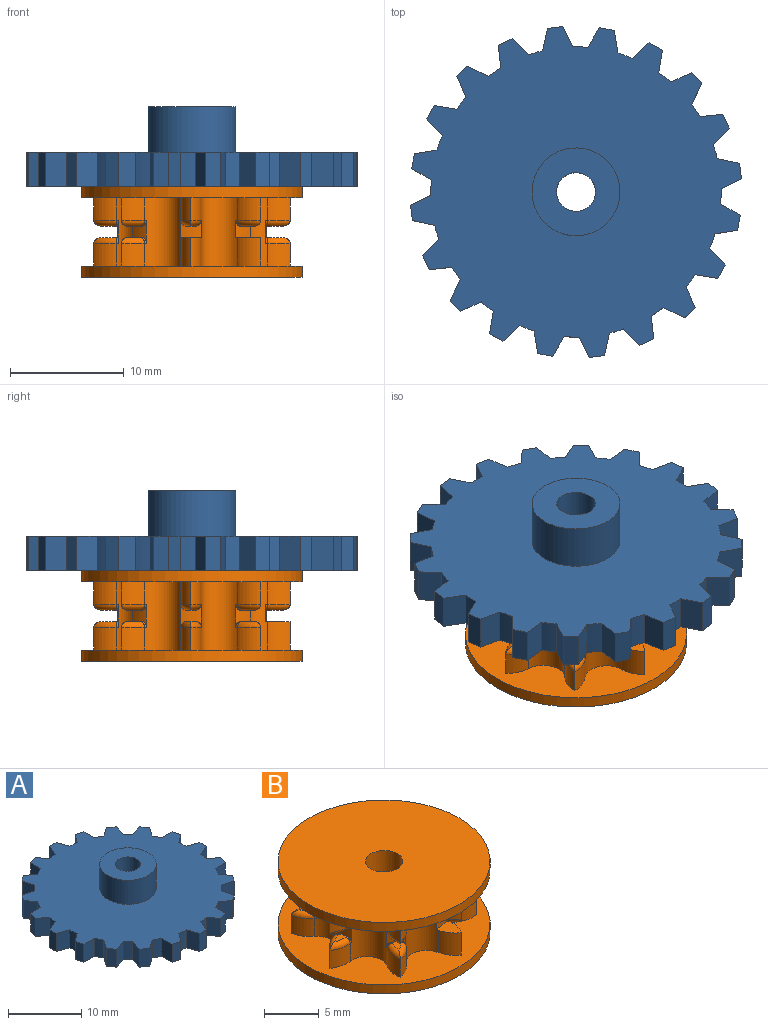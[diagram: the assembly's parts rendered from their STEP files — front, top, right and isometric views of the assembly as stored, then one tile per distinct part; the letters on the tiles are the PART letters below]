
ASSEMBLY  parts=2 mates=1
PART A: 85 faces, bbox 29.1x29.1x7 mm
  f0: plane 3x1.89mm, normal (-0.94,0.33,0), area 6mm2, adj f2,f3,f4,f5
  f1: plane 3x1.89mm, normal (0.94,0.33,0), area 6mm2, adj f2,f3,f4,f81
  f2: plane 3x1.33mm, normal (0,1,0), area 4mm2, adj f0,f1,f3,f4
  f3: plane 29.1x29.1mm, normal (0,0,1), area 535.5mm2, adj f0,f1,f2,f5,f6,f7,f8,f9
  f4: plane 29.1x29.1mm, normal (0,0,-1), area 573.2mm2, adj f0,f1,f2,f5,f6,f7,f8,f9
  f5: cylinder r=12.73mm len=3mm, axis (0,0,-1), area 4mm2, adj f0,f3,f4,f7
  f6: plane 3x2mm, normal (-1,0.03,0), area 6mm2, adj f3,f4,f8,f9
  f7: plane 3x1.59mm, normal (0.79,0.61,0), area 6mm2, adj f3,f4,f5,f8
  f8: plane 3x1.27mm, normal (-0.31,0.95,0), area 4mm2, adj f3,f4,f6,f7
  f9: cylinder r=12.73mm len=3mm, axis (0,0,-1), area 4mm2, adj f3,f4,f6,f11
  f10: plane 3x1.92mm, normal (-0.96,-0.28,0), area 6mm2, adj f3,f4,f12,f13
  f11: plane 3x1.65mm, normal (0.57,0.82,0), area 6mm2, adj f3,f4,f9,f12
  f12: plane 3x1.08mm, normal (-0.59,0.81,0), area 4mm2, adj f3,f4,f10,f11
  f13: cylinder r=12.73mm len=3mm, axis (0,0,-1), area 4mm2, adj f3,f4,f10,f15
  f14: plane 3x1.65mm, normal (-0.82,-0.57,0), area 6mm2, adj f3,f4,f16,f17
  f15: plane 3x1.92mm, normal (0.28,0.96,0), area 6mm2, adj f3,f4,f13,f16
  f16: plane 3x1.08mm, normal (-0.81,0.59,0), area 4mm2, adj f3,f4,f14,f15
  f17: cylinder r=12.73mm len=3mm, axis (0,0,-1), area 4mm2, adj f3,f4,f14,f19
  f18: plane 3x1.59mm, normal (-0.61,-0.79,0), area 6mm2, adj f3,f4,f20,f21
  f19: plane 3x2mm, normal (-0.03,1,0), area 6mm2, adj f3,f4,f17,f20
  f20: plane 3x1.27mm, normal (-0.95,0.31,0), area 4mm2, adj f3,f4,f18,f19
  f21: cylinder r=12.73mm len=3mm, axis (0,0,-1), area 4mm2, adj f3,f4,f18,f23
  f22: plane 3x1.89mm, normal (-0.33,-0.94,0), area 6mm2, adj f3,f4,f24,f25
  f23: plane 3x1.89mm, normal (-0.33,0.94,0), area 6mm2, adj f3,f4,f21,f24
  f24: plane 3x1.33mm, normal (-1,0,0), area 4mm2, adj f3,f4,f22,f23
  f25: cylinder r=12.73mm len=3mm, axis (0,0,-1), area 4mm2, adj f3,f4,f22,f27
  f26: plane 3x2mm, normal (-0.03,-1,0), area 6mm2, adj f3,f4,f28,f29
  f27: plane 3x1.59mm, normal (-0.61,0.79,0), area 6mm2, adj f3,f4,f25,f28
  f28: plane 3x1.27mm, normal (-0.95,-0.31,0), area 4mm2, adj f3,f4,f26,f27
  f29: cylinder r=12.73mm len=3mm, axis (0,0,-1), area 4mm2, adj f3,f4,f26,f31
  f30: plane 3x1.92mm, normal (0.28,-0.96,0), area 6mm2, adj f3,f4,f32,f33
  f31: plane 3x1.65mm, normal (-0.82,0.57,0), area 6mm2, adj f3,f4,f29,f32
  f32: plane 3x1.08mm, normal (-0.81,-0.59,0), area 4mm2, adj f3,f4,f30,f31
  f33: cylinder r=12.73mm len=3mm, axis (0,0,-1), area 4mm2, adj f3,f4,f30,f35
  f34: plane 3x1.65mm, normal (0.57,-0.82,0), area 6mm2, adj f3,f4,f36,f37
  f35: plane 3x1.92mm, normal (-0.96,0.28,0), area 6mm2, adj f3,f4,f33,f36
  f36: plane 3x1.08mm, normal (-0.59,-0.81,0), area 4mm2, adj f3,f4,f34,f35
  f37: cylinder r=12.73mm len=3mm, axis (0,0,-1), area 4mm2, adj f3,f4,f34,f39
  f38: plane 3x1.59mm, normal (0.79,-0.61,0), area 6mm2, adj f3,f4,f40,f41
  f39: plane 3x2mm, normal (-1,-0.03,0), area 6mm2, adj f3,f4,f37,f40
  f40: plane 3x1.27mm, normal (-0.31,-0.95,0), area 4mm2, adj f3,f4,f38,f39
  f41: cylinder r=12.73mm len=3mm, axis (0,0,-1), area 4mm2, adj f3,f4,f38,f43
  f42: plane 3x1.89mm, normal (0.94,-0.33,0), area 6mm2, adj f3,f4,f44,f45
  f43: plane 3x1.89mm, normal (-0.94,-0.33,0), area 6mm2, adj f3,f4,f41,f44
  f44: plane 3x1.33mm, normal (0,-1,0), area 4mm2, adj f3,f4,f42,f43
  f45: cylinder r=12.73mm len=3mm, axis (0,0,-1), area 4mm2, adj f3,f4,f42,f47
  f46: plane 3x2mm, normal (1,-0.03,0), area 6mm2, adj f3,f4,f48,f49
  f47: plane 3x1.59mm, normal (-0.79,-0.61,0), area 6mm2, adj f3,f4,f45,f48
  f48: plane 3x1.27mm, normal (0.31,-0.95,0), area 4mm2, adj f3,f4,f46,f47
  f49: cylinder r=12.73mm len=3mm, axis (0,0,-1), area 4mm2, adj f3,f4,f46,f51
  f50: plane 3x1.92mm, normal (0.96,0.28,0), area 6mm2, adj f3,f4,f52,f53
  f51: plane 3x1.65mm, normal (-0.57,-0.82,0), area 6mm2, adj f3,f4,f49,f52
  f52: plane 3x1.08mm, normal (0.59,-0.81,0), area 4mm2, adj f3,f4,f50,f51
  f53: cylinder r=12.73mm len=3mm, axis (0,0,-1), area 4mm2, adj f3,f4,f50,f55
  f54: plane 3x1.65mm, normal (0.82,0.57,0), area 6mm2, adj f3,f4,f56,f57
  f55: plane 3x1.92mm, normal (-0.28,-0.96,0), area 6mm2, adj f3,f4,f53,f56
  f56: plane 3x1.08mm, normal (0.81,-0.59,0), area 4mm2, adj f3,f4,f54,f55
  f57: cylinder r=12.73mm len=3mm, axis (0,0,-1), area 4mm2, adj f3,f4,f54,f59
  f58: plane 3x1.59mm, normal (0.61,0.79,0), area 6mm2, adj f3,f4,f60,f61
  f59: plane 3x2mm, normal (0.03,-1,0), area 6mm2, adj f3,f4,f57,f60
  f60: plane 3x1.27mm, normal (0.95,-0.31,0), area 4mm2, adj f3,f4,f58,f59
  f61: cylinder r=12.73mm len=3mm, axis (0,0,-1), area 4mm2, adj f3,f4,f58,f63
  f62: plane 3x1.89mm, normal (0.33,0.94,0), area 6mm2, adj f3,f4,f64,f65
  f63: plane 3x1.89mm, normal (0.33,-0.94,0), area 6mm2, adj f3,f4,f61,f64
  f64: plane 3x1.33mm, normal (1,0,0), area 4mm2, adj f3,f4,f62,f63
  f65: cylinder r=12.73mm len=3mm, axis (0,0,-1), area 4mm2, adj f3,f4,f62,f67
  f66: plane 3x2mm, normal (0.03,1,0), area 6mm2, adj f3,f4,f68,f69
  f67: plane 3x1.59mm, normal (0.61,-0.79,0), area 6mm2, adj f3,f4,f65,f68
  f68: plane 3x1.27mm, normal (0.95,0.31,0), area 4mm2, adj f3,f4,f66,f67
  f69: cylinder r=12.73mm len=3mm, axis (0,0,-1), area 4mm2, adj f3,f4,f66,f71
  f70: plane 3x1.92mm, normal (-0.28,0.96,0), area 6mm2, adj f3,f4,f72,f73
  f71: plane 3x1.65mm, normal (0.82,-0.57,0), area 6mm2, adj f3,f4,f69,f72
  f72: plane 3x1.08mm, normal (0.81,0.59,0), area 4mm2, adj f3,f4,f70,f71
  f73: cylinder r=12.73mm len=3mm, axis (0,0,-1), area 4mm2, adj f3,f4,f70,f75
  f74: plane 3x1.65mm, normal (-0.57,0.82,0), area 6mm2, adj f3,f4,f76,f77
  f75: plane 3x1.92mm, normal (0.96,-0.28,0), area 6mm2, adj f3,f4,f73,f76
  f76: plane 3x1.08mm, normal (0.59,0.81,0), area 4mm2, adj f3,f4,f74,f75
  f77: cylinder r=12.73mm len=3mm, axis (0,0,-1), area 4mm2, adj f3,f4,f74,f79
  f78: plane 3x1.59mm, normal (-0.79,0.61,0), area 6mm2, adj f3,f4,f80,f81
  f79: plane 3x2mm, normal (1,0.03,0), area 6mm2, adj f3,f4,f77,f80
  f80: plane 3x1.27mm, normal (0.31,0.95,0), area 4mm2, adj f3,f4,f78,f79
  f81: cylinder r=12.73mm len=3mm, axis (0,0,-1), area 4mm2, adj f1,f3,f4,f78
  f82: cylinder r=1.7mm len=7mm, axis (0,0,-1), area 74.8mm2, adj f4,f84
  f83: cylinder r=3.86mm len=7.71mm, axis (0,0,-1), area 96.9mm2, adj f3,f84
  f84: plane 7.71x7.71mm, normal (0,0,1), area 37.7mm2, adj f82,f83
PART B: 127 faces, bbox 19.4x19.4x8 mm
  f0: cylinder r=2.85mm len=2.12mm, axis (0,0,1), area 4.4mm2, adj f2,f23,f42,f92
  f1: cylinder r=2.85mm len=2.09mm, axis (0,0,1), area 4.4mm2, adj f2,f3,f42,f72
  f2: cylinder r=1.9mm len=6mm, axis (0,0,1), area 25.3mm2, adj f0,f1,f24,f25,f42,f43,f48,f67
  f3: cylinder r=2.85mm len=2mm, axis (0,0,1), area 4.4mm2, adj f1,f4,f42,f71
  f4: cylinder r=1.9mm len=6mm, axis (0,0,1), area 25.4mm2, adj f3,f5,f27,f28,f42,f43,f65,f66
  f5: cylinder r=2.85mm len=2.5mm, axis (0,0,1), area 5.5mm2, adj f4,f6,f42,f65
  f6: cylinder r=2.85mm len=2.5mm, axis (0,0,1), area 5.5mm2, adj f5,f7,f42,f65
  f7: cylinder r=1.9mm len=6mm, axis (0,0,1), area 25.5mm2, adj f6,f8,f29,f30,f42,f43,f62,f63
  f8: cylinder r=2.85mm len=2.5mm, axis (0,0,1), area 5.5mm2, adj f7,f9,f42,f62
  f9: cylinder r=2.85mm len=2.5mm, axis (0,0,1), area 5.5mm2, adj f8,f10,f42,f62
  f10: cylinder r=1.9mm len=6mm, axis (0,0,1), area 25.4mm2, adj f9,f11,f31,f32,f42,f43,f60,f62
  f11: cylinder r=2.85mm len=2mm, axis (0,0,1), area 4.4mm2, adj f10,f12,f42,f76
  f12: cylinder r=2.85mm len=2.12mm, axis (0,0,1), area 4.4mm2, adj f11,f13,f42,f75
  f13: cylinder r=1.9mm len=6mm, axis (0,0,1), area 25.3mm2, adj f12,f14,f33,f34,f42,f43,f57,f60
  f14: cylinder r=2.85mm len=2.09mm, axis (0,0,1), area 4.4mm2, adj f13,f15,f42,f80
  f15: cylinder r=2.85mm len=2mm, axis (0,0,1), area 4.4mm2, adj f14,f16,f42,f79
  f16: cylinder r=1.9mm len=6mm, axis (0,0,1), area 25.3mm2, adj f15,f17,f35,f36,f42,f43,f54,f57
  f17: cylinder r=2.85mm len=2mm, axis (0,0,1), area 4.4mm2, adj f16,f18,f42,f84
  f18: cylinder r=2.85mm len=2.12mm, axis (0,0,1), area 4.4mm2, adj f17,f19,f42,f83
  f19: cylinder r=1.9mm len=6mm, axis (0,0,1), area 25.3mm2, adj f18,f20,f37,f38,f42,f43,f51,f54
  f20: cylinder r=2.85mm len=2.09mm, axis (0,0,1), area 4.4mm2, adj f19,f21,f42,f88
  f21: cylinder r=2.85mm len=2mm, axis (0,0,1), area 4.4mm2, adj f20,f22,f42,f87
  f22: cylinder r=1.9mm len=6mm, axis (0,0,1), area 25.3mm2, adj f21,f23,f42,f43,f44,f45,f48,f51
  f23: cylinder r=2.85mm len=2mm, axis (0,0,1), area 4.4mm2, adj f0,f22,f42,f91
  f24: cylinder r=2.85mm len=2.12mm, axis (0,0,1), area 4.4mm2, adj f2,f43,f45,f124
  f25: cylinder r=2.85mm len=2.09mm, axis (0,0,1), area 4.4mm2, adj f2,f27,f43,f96
  f26: cylinder r=9.7mm len=19.4mm, axis (0,0,-1), area 60.9mm2, adj f40,f43
  f27: cylinder r=2.85mm len=2mm, axis (0,0,1), area 4.4mm2, adj f4,f25,f43,f95
  f28: cylinder r=2.85mm len=2mm, axis (0,0,1), area 4.4mm2, adj f4,f29,f43,f100
  f29: cylinder r=2.85mm len=2.12mm, axis (0,0,1), area 4.4mm2, adj f7,f28,f43,f99
  f30: cylinder r=2.85mm len=2.09mm, axis (0,0,1), area 4.4mm2, adj f7,f31,f43,f104
  f31: cylinder r=2.85mm len=2mm, axis (0,0,1), area 4.4mm2, adj f10,f30,f43,f103
  f32: cylinder r=2.85mm len=2mm, axis (0,0,1), area 4.4mm2, adj f10,f33,f43,f108
  f33: cylinder r=2.85mm len=2.12mm, axis (0,0,1), area 4.4mm2, adj f13,f32,f43,f107
  f34: cylinder r=2.85mm len=2.09mm, axis (0,0,1), area 4.4mm2, adj f13,f35,f43,f112
  f35: cylinder r=2.85mm len=2mm, axis (0,0,1), area 4.4mm2, adj f16,f34,f43,f111
  f36: cylinder r=2.85mm len=2mm, axis (0,0,1), area 4.4mm2, adj f16,f37,f43,f116
  f37: cylinder r=2.85mm len=2.12mm, axis (0,0,1), area 4.4mm2, adj f19,f36,f43,f115
  f38: cylinder r=2.85mm len=2.09mm, axis (0,0,1), area 4.4mm2, adj f19,f43,f44,f120
  f39: cylinder r=9.7mm len=19.4mm, axis (0,0,-1), area 60.9mm2, adj f41,f42
  f40: plane 19.4x19.4mm, normal (0,0,1), area 286.4mm2, adj f26,f126
  f41: plane 19.4x19.4mm, normal (0,0,-1), area 286.4mm2, adj f39,f126
  f42: plane 19.4x19.4mm, normal (0,0,1), area 162.6mm2, adj f0,f1,f2,f3,f4,f5,f6,f7
  f43: plane 19.4x19.4mm, normal (0,0,-1), area 162.6mm2, adj f2,f4,f7,f10,f13,f16,f19,f22
  f44: cylinder r=2.85mm len=2mm, axis (0,0,1), area 4.4mm2, adj f22,f38,f43,f119
  f45: cylinder r=2.85mm len=2mm, axis (0,0,1), area 4.4mm2, adj f22,f24,f43,f123
  f46: plane 1.33x1.09mm, normal (0,0,1), area 0.7mm2, adj f48,f90,f91,f92,f93
  f47: plane 1.33x1.09mm, normal (0,0,-1), area 0.7mm2, adj f48,f122,f123,f124,f125
  f48: cylinder r=6.5mm len=2mm, axis (0,0,1), area 2mm2, adj f2,f22,f46,f47,f90,f93,f122,f125
  f49: plane 1.4x0.8mm, normal (0,0,-1), area 0.7mm2, adj f51,f118,f119,f120,f121
  f50: plane 1.4x0.8mm, normal (0,0,1), area 0.7mm2, adj f51,f86,f87,f88,f89
  f51: cylinder r=6.5mm len=2mm, axis (0,0,1), area 2mm2, adj f19,f22,f49,f50,f86,f89,f118,f121
  f52: plane 1.33x1.09mm, normal (0,0,-1), area 0.7mm2, adj f54,f114,f115,f116,f117
  f53: plane 1.33x1.09mm, normal (0,0,1), area 0.7mm2, adj f54,f82,f83,f84,f85
  f54: cylinder r=6.5mm len=2mm, axis (0,0,1), area 2mm2, adj f16,f19,f52,f53,f82,f85,f114,f117
  f55: plane 1.4x0.8mm, normal (0,0,-1), area 0.7mm2, adj f57,f110,f111,f112,f113
  f56: plane 1.4x0.8mm, normal (0,0,1), area 0.7mm2, adj f57,f78,f79,f80,f81
  f57: cylinder r=6.5mm len=2mm, axis (0,0,1), area 2mm2, adj f13,f16,f55,f56,f78,f81,f110,f113
  f58: plane 1.33x1.09mm, normal (0,0,-1), area 0.7mm2, adj f60,f106,f107,f108,f109
  f59: plane 1.33x1.09mm, normal (0,0,1), area 0.7mm2, adj f60,f74,f75,f76,f77
  f60: cylinder r=6.5mm len=2mm, axis (0,0,1), area 2mm2, adj f10,f13,f58,f59,f74,f77,f106,f109
  f61: plane 1.4x0.8mm, normal (0,0,-1), area 0.7mm2, adj f63,f102,f103,f104,f105
  f62: plane 2.3x1.81mm, normal (0,0,1), area 2.6mm2, adj f7,f8,f9,f10,f63
  f63: cylinder r=6.5mm len=1.77mm, axis (0,0,1), area 1.9mm2, adj f7,f10,f61,f62,f102,f105
  f64: plane 1.33x1.09mm, normal (0,0,-1), area 0.7mm2, adj f66,f98,f99,f100,f101
  f65: plane 2.3x2.04mm, normal (0,0,1), area 2.6mm2, adj f4,f5,f6,f7,f66
  f66: cylinder r=6.5mm len=1.5mm, axis (0,0,1), area 1.9mm2, adj f4,f7,f64,f65,f98,f101
  f67: cylinder r=6.5mm len=2mm, axis (0,0,1), area 2mm2, adj f2,f4,f68,f69,f70,f73,f94,f97
  f68: plane 1.4x0.8mm, normal (0,0,1), area 0.7mm2, adj f67,f70,f71,f72,f73
  f69: plane 1.4x0.8mm, normal (0,0,-1), area 0.7mm2, adj f67,f94,f95,f96,f97
  f70: torus R=2.4mm, axis (0,0,1), area 0.1mm2, adj f4,f67,f68,f71
  f71: torus R=2.35mm, axis (0,0,1), area 1.5mm2, adj f3,f68,f70,f72
  f72: torus R=2.35mm, axis (0,0,1), area 1.5mm2, adj f1,f68,f71,f73
  f73: torus R=2.4mm, axis (0,0,1), area 0.1mm2, adj f2,f67,f68,f72
  f74: torus R=2.4mm, axis (0,0,1), area 0.1mm2, adj f13,f59,f60,f75
  f75: torus R=2.35mm, axis (0,0,1), area 1.5mm2, adj f12,f59,f74,f76
  f76: torus R=2.35mm, axis (0,0,1), area 1.5mm2, adj f11,f59,f75,f77
  f77: torus R=2.4mm, axis (0,0,1), area 0.1mm2, adj f10,f59,f60,f76
  f78: torus R=2.4mm, axis (0,0,1), area 0.1mm2, adj f16,f56,f57,f79
  f79: torus R=2.35mm, axis (0,0,1), area 1.5mm2, adj f15,f56,f78,f80
  f80: torus R=2.35mm, axis (0,0,1), area 1.5mm2, adj f14,f56,f79,f81
  f81: torus R=2.4mm, axis (0,0,1), area 0.1mm2, adj f13,f56,f57,f80
  f82: torus R=2.4mm, axis (0,0,1), area 0.1mm2, adj f19,f53,f54,f83
  f83: torus R=2.35mm, axis (0,0,1), area 1.5mm2, adj f18,f53,f82,f84
  f84: torus R=2.35mm, axis (0,0,1), area 1.5mm2, adj f17,f53,f83,f85
  f85: torus R=2.4mm, axis (0,0,1), area 0.1mm2, adj f16,f53,f54,f84
  f86: torus R=2.4mm, axis (0,0,1), area 0.1mm2, adj f22,f50,f51,f87
  f87: torus R=2.35mm, axis (0,0,1), area 1.5mm2, adj f21,f50,f86,f88
  f88: torus R=2.35mm, axis (0,0,1), area 1.5mm2, adj f20,f50,f87,f89
  f89: torus R=2.4mm, axis (0,0,1), area 0.1mm2, adj f19,f50,f51,f88
  f90: torus R=2.4mm, axis (0,0,1), area 0.1mm2, adj f22,f46,f48,f91
  f91: torus R=2.35mm, axis (0,0,1), area 1.5mm2, adj f23,f46,f90,f92
  f92: torus R=2.35mm, axis (0,0,1), area 1.5mm2, adj f0,f46,f91,f93
  f93: torus R=2.4mm, axis (0,0,1), area 0.1mm2, adj f2,f46,f48,f92
  f94: torus R=2.4mm, axis (0,0,1), area 0.1mm2, adj f4,f67,f69,f95
  f95: torus R=2.35mm, axis (0,0,1), area 1.5mm2, adj f27,f69,f94,f96
  f96: torus R=2.35mm, axis (0,0,1), area 1.5mm2, adj f25,f69,f95,f97
  f97: torus R=2.4mm, axis (0,0,1), area 0.1mm2, adj f2,f67,f69,f96
  f98: torus R=2.4mm, axis (0,0,1), area 0.1mm2, adj f7,f64,f66,f99
  f99: torus R=2.35mm, axis (0,0,1), area 1.5mm2, adj f29,f64,f98,f100
  f100: torus R=2.35mm, axis (0,0,1), area 1.5mm2, adj f28,f64,f99,f101
  f101: torus R=2.4mm, axis (0,0,1), area 0.1mm2, adj f4,f64,f66,f100
  f102: torus R=2.4mm, axis (0,0,1), area 0.1mm2, adj f10,f61,f63,f103
  f103: torus R=2.35mm, axis (0,0,1), area 1.5mm2, adj f31,f61,f102,f104
  f104: torus R=2.35mm, axis (0,0,1), area 1.5mm2, adj f30,f61,f103,f105
  f105: torus R=2.4mm, axis (0,0,1), area 0.1mm2, adj f7,f61,f63,f104
  f106: torus R=2.4mm, axis (0,0,1), area 0.1mm2, adj f13,f58,f60,f107
  f107: torus R=2.35mm, axis (0,0,1), area 1.5mm2, adj f33,f58,f106,f108
  f108: torus R=2.35mm, axis (0,0,1), area 1.5mm2, adj f32,f58,f107,f109
  f109: torus R=2.4mm, axis (0,0,1), area 0.1mm2, adj f10,f58,f60,f108
  f110: torus R=2.4mm, axis (0,0,1), area 0.1mm2, adj f16,f55,f57,f111
  f111: torus R=2.35mm, axis (0,0,1), area 1.5mm2, adj f35,f55,f110,f112
  f112: torus R=2.35mm, axis (0,0,1), area 1.5mm2, adj f34,f55,f111,f113
  f113: torus R=2.4mm, axis (0,0,1), area 0.1mm2, adj f13,f55,f57,f112
  f114: torus R=2.4mm, axis (0,0,1), area 0.1mm2, adj f19,f52,f54,f115
  f115: torus R=2.35mm, axis (0,0,1), area 1.5mm2, adj f37,f52,f114,f116
  f116: torus R=2.35mm, axis (0,0,1), area 1.5mm2, adj f36,f52,f115,f117
  f117: torus R=2.4mm, axis (0,0,1), area 0.1mm2, adj f16,f52,f54,f116
  f118: torus R=2.4mm, axis (0,0,1), area 0.1mm2, adj f22,f49,f51,f119
  f119: torus R=2.35mm, axis (0,0,1), area 1.5mm2, adj f44,f49,f118,f120
  f120: torus R=2.35mm, axis (0,0,1), area 1.5mm2, adj f38,f49,f119,f121
  f121: torus R=2.4mm, axis (0,0,1), area 0.1mm2, adj f19,f49,f51,f120
  f122: torus R=2.4mm, axis (0,0,1), area 0.1mm2, adj f22,f47,f48,f123
  f123: torus R=2.35mm, axis (0,0,1), area 1.5mm2, adj f45,f47,f122,f124
  f124: torus R=2.35mm, axis (0,0,1), area 1.5mm2, adj f24,f47,f123,f125
  f125: torus R=2.4mm, axis (0,0,1), area 0.1mm2, adj f2,f47,f48,f124
  f126: cylinder r=1.7mm len=8mm, axis (0,0,-1), area 85.5mm2, adj f40,f41
PLACE A rot(axis=(0,0,-1),10.7deg) t=(-107.51,59.69,67.05)mm
PLACE B rot(axis=(0,0,-1),10.7deg) t=(-32.5,-11.78,59.05)mm
MATE fastened B.f26 <-> A.f5  axis (0,0,1) through (-79.82,8.78,67.05)mm
